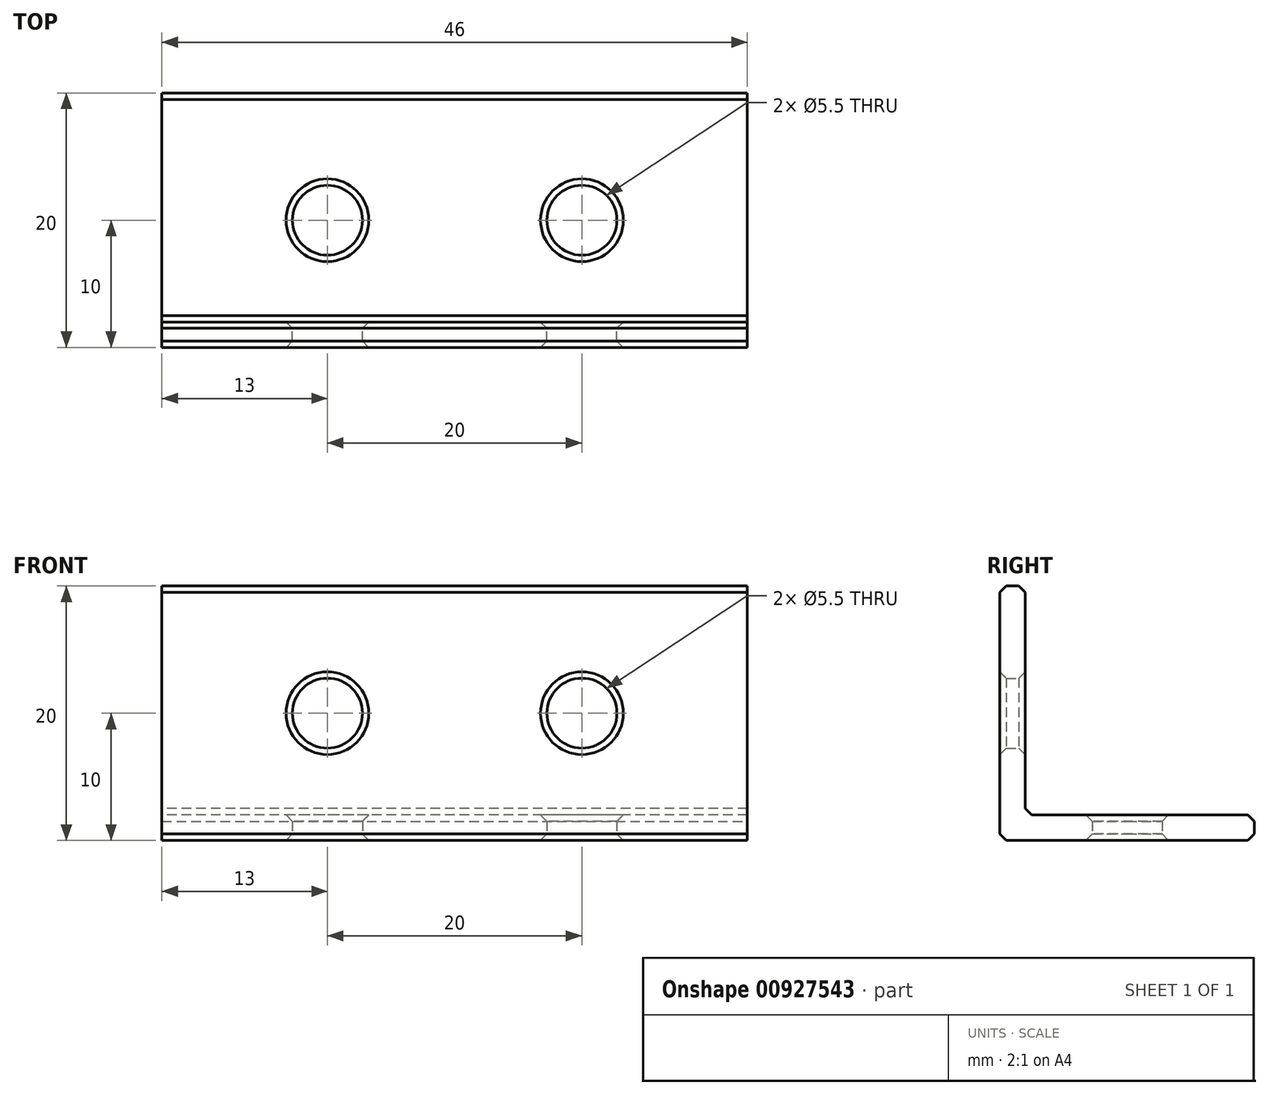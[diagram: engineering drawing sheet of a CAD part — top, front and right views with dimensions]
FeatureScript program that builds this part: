
annotation { "Feature Type Name" : "Feature", "Feature Type Description" : "" }
export const myFeature = defineFeature(function(context is Context, id is Id, definition is map)
    precondition{}
    {
        {
            var Q0;
            Q0=qCreatedBy(makeId("Right.planeOp"),FACE);
            var sketch = newSketch(context, id + "F0", { "sketchPlane" : qUnion([Q0])});
            skLineSegment(sketch, "E0", {"start": v(0, 0) * mm, "end": v(18, 0) * mm});
            skLineSegment(sketch, "E1", {"start": v(0, 18) * mm, "end": v(0, 0) * mm});
            skLineSegment(sketch, "E2", {"start": v(0, 18) * mm, "end": v(-2, 18) * mm});
            skLineSegment(sketch, "E3", {"start": v(-2, 18) * mm, "end": v(-2, -2) * mm});
            skLineSegment(sketch, "E4", {"start": v(-2, -2) * mm, "end": v(18, -2) * mm});
            skLineSegment(sketch, "E5", {"start": v(18, -2) * mm, "end": v(18, 0) * mm});
            skSolve(sketch);
        }
        {
            var Q0;
            Q0 = qSketchRegion(id + "F0", true);
            extrude(context, id + "F1", {"entities" : qUnion([Q0]), "depth" : 50 * mm, "offsetDistance" : 25 * mm});
        }
        {
            var Q0;
            Q0=makeQuery(id+"F1.opExtrude","SWEPT_FACE",FACE,{"disambiguationData":[OSD([sQuery(id+"F0.wireOp",EDGE,"E2")])]});
            var Q1;
            Q1=makeQuery(id+"F1.opExtrude","SWEPT_FACE",FACE,{"disambiguationData":[OSD([sQuery(id+"F0.wireOp",EDGE,"E0")])]});
            var Q2;
            Q2=makeQuery(id+"F1.opExtrude","SWEPT_FACE",FACE,{"disambiguationData":[OSD([sQuery(id+"F0.wireOp",EDGE,"E4")])]});
            var Q3;
            Q3=makeQuery(id+"F1.opExtrude","SWEPT_FACE",FACE,{"disambiguationData":[OSD([sQuery(id+"F0.wireOp",EDGE,"E3")])]});
            chamfer(context, id + "F2", {"entities" : qUnion([Q0, Q1, Q2, Q3]), "width" : 0.5 * mm, "tangentPropagation" : true});
        }
        {
            var Q0;
            Q0=makeQuery(id+"F1.opExtrude","SWEPT_FACE",FACE,{"disambiguationData":[OSD([sQuery(id+"F0.wireOp",EDGE,"E1")])]});
            var sketch = newSketch(context, id + "F3", { "sketchPlane" : qUnion([Q0])});
            skLineSegment(sketch, "E6", {"start": v(73.44, 8) * mm, "end": v(-128.85, 8) * mm, "construction": true});
            skCircle(sketch, "E7", {"center": v(-15, 8) * mm, "radius": 2.75 * mm});
            skCircle(sketch, "E8", {"center": v(-35, 8) * mm, "radius": 2.75 * mm});
            skSolve(sketch);
        }
        {
            var Q0;
            Q0 = qSketchRegion(id + "F3", true);
            extrude(context, id + "F4", {"entities" : qUnion([Q0]), "operationType" : NewBodyOperationType.REMOVE, "oppositeDirection" : true, "depth" : 25 * mm, "offsetDistance" : 25 * mm});
        }
        {
            var Q0;
            Q0=makeQuery(id+"F4.boolean.opBoolean","COPY",FACE,{"derivedFrom":makeQuery(id+"F4.opExtrude","SWEPT_FACE",FACE,{"disambiguationData":[OSD([sQuery(id+"F3.wireOp",EDGE,"E7")])]})});
            var Q1;
            Q1=makeQuery(id+"F4.boolean.opBoolean","COPY",FACE,{"derivedFrom":makeQuery(id+"F4.opExtrude","SWEPT_FACE",FACE,{"disambiguationData":[OSD([sQuery(id+"F3.wireOp",EDGE,"E8")])]})});
            chamfer(context, id + "F5", {"entities" : qUnion([Q0, Q1]), "width" : 0.5 * mm, "tangentPropagation" : true});
        }
        {
            var Q0;
            Q0=makeQuery(id+"F1.opExtrude","SWEPT_FACE",FACE,{"disambiguationData":[OSD([sQuery(id+"F0.wireOp",EDGE,"E4")])]});
            var sketch = newSketch(context, id + "F6", { "sketchPlane" : qUnion([Q0])});
            skLineSegment(sketch, "E9", {"start": v(-42.84, -8) * mm, "end": v(93.15, -8) * mm, "construction": true});
            skCircle(sketch, "E10", {"center": v(15, -8) * mm, "radius": 2.75 * mm});
            skCircle(sketch, "E11", {"center": v(35, -8) * mm, "radius": 2.75 * mm});
            skSolve(sketch);
        }
        {
            var Q0;
            Q0 = qSketchRegion(id + "F6", true);
            extrude(context, id + "F7", {"entities" : qUnion([Q0]), "operationType" : NewBodyOperationType.REMOVE, "oppositeDirection" : true, "depth" : 25 * mm, "offsetDistance" : 25 * mm});
        }
        {
            var Q0;
            Q0=makeQuery(id+"F7.boolean.opBoolean","COPY",FACE,{"derivedFrom":makeQuery(id+"F7.opExtrude","SWEPT_FACE",FACE,{"disambiguationData":[OSD([sQuery(id+"F6.wireOp",EDGE,"E10")])]})});
            var Q1;
            Q1=makeQuery(id+"F7.boolean.opBoolean","COPY",FACE,{"derivedFrom":makeQuery(id+"F7.opExtrude","SWEPT_FACE",FACE,{"disambiguationData":[OSD([sQuery(id+"F6.wireOp",EDGE,"E11")])]})});
            chamfer(context, id + "F8", {"entities" : qUnion([Q0, Q1]), "width" : 0.5 * mm, "tangentPropagation" : true});
        }
        {
            var Q0;
            Q0=makeQuery(id+"F1.opExtrude","SWEPT_FACE",FACE,{"disambiguationData":[OSD([sQuery(id+"F0.wireOp",EDGE,"E3")])]});
            var sketch = newSketch(context, id + "F9", { "sketchPlane" : qUnion([Q0])});
            skLineSegment(sketch, "E12", {"start": v(25, 24.5) * mm, "end": v(25, -8.38) * mm, "construction": true});
            skPoint(sketch, "E12.startSnap0", {"position": v(25, 17.5) * mm});
            skLineSegment(sketch, "E13.bottom", {"start": v(2, 18) * mm, "end": v(48, 18) * mm});
            skLineSegment(sketch, "E13.top", {"start": v(2, -2) * mm, "end": v(48, -2) * mm});
            skLineSegment(sketch, "E13.left", {"start": v(2, 18) * mm, "end": v(2, -2) * mm});
            skLineSegment(sketch, "E13.right", {"start": v(48, 18) * mm, "end": v(48, -2) * mm});
            skLineSegment(sketch, "E14.bottom", {"start": v(-2.29, 19.67) * mm, "end": v(2, 19.67) * mm});
            skLineSegment(sketch, "E14.top", {"start": v(-2.29, -2) * mm, "end": v(2, -2) * mm});
            skLineSegment(sketch, "E14.left", {"start": v(-2.29, 19.67) * mm, "end": v(-2.29, -2) * mm});
            skLineSegment(sketch, "E14.right", {"start": v(2, 19.67) * mm, "end": v(2, -2) * mm});
            skLineSegment(sketch, "E15.bottom", {"start": v(48, 18) * mm, "end": v(51.75, 18) * mm});
            skLineSegment(sketch, "E15.top", {"start": v(48, -2.04) * mm, "end": v(51.75, -2.04) * mm});
            skLineSegment(sketch, "E15.left", {"start": v(48, 18) * mm, "end": v(48, -2.04) * mm});
            skLineSegment(sketch, "E15.right", {"start": v(51.75, 18) * mm, "end": v(51.75, -2.04) * mm});
            skSolve(sketch);
        }
        {
            var Q0;
            {var subQ7=sQuery(id+"F9.wireOp",EDGE,"E15.bottom");Q0=makeQuery(id+"F9.imprint","IMPRINT",FACE,{"disambiguationData":[TD([[makeQuery(id+"F9.imprint","IMPRINT",EDGE,{"derivedFrom":subQ7}),-1.0]])]});}
            var Q1;
            {var subQ1=sQuery(id+"F0.wireOp",EDGE,"E3");var subQ2=makeQuery(id+"F1.opExtrude","SWEPT_FACE",FACE,{"disambiguationData":[OSD([subQ1])]});var subQ7=makeQuery(id+"F2.opChamfer","BLEND_EDGE",EDGE,{"blendedFrom":[makeQuery(id+"F1.opExtrude","CAP_EDGE",EDGE,{"disambiguationData":[OSD([subQ1])],"isStart":false}),subQ2],"blendedInto":[subQ2]});Q1=makeQuery(id+"F9.imprint","IMPRINT",FACE,{"disambiguationData":[TD([[makeQuery(id+"F9.imprint","IMPRINT",EDGE,{"derivedFrom":subQ7}),1.0]])]});}
            var Q2;
            {var subQ2=sQuery(id+"F9.wireOp",EDGE,"E14.bottom");Q2=makeQuery(id+"F9.imprint","IMPRINT",FACE,{"disambiguationData":[TD([[makeQuery(id+"F9.imprint","IMPRINT",EDGE,{"derivedFrom":subQ2}),-1.0]])]});}
            var Q3;
            {var subQ1=sQuery(id+"F0.wireOp",EDGE,"E3");var subQ2=makeQuery(id+"F1.opExtrude","SWEPT_FACE",FACE,{"disambiguationData":[OSD([subQ1])]});var subQ7=makeQuery(id+"F2.opChamfer","BLEND_EDGE",EDGE,{"blendedFrom":[makeQuery(id+"F1.opExtrude","CAP_EDGE",EDGE,{"disambiguationData":[OSD([subQ1])],"isStart":true}),subQ2],"blendedInto":[subQ2]});Q3=makeQuery(id+"F9.imprint","IMPRINT",FACE,{"disambiguationData":[TD([[makeQuery(id+"F9.imprint","IMPRINT",EDGE,{"derivedFrom":subQ7}),1.0]])]});}
            extrude(context, id + "F10", {"entities" : qUnion([Q0, Q1, Q2, Q3]), "operationType" : NewBodyOperationType.REMOVE, "oppositeDirection" : true, "depth" : 25 * mm, "offsetDistance" : 25 * mm});
        }
    });
